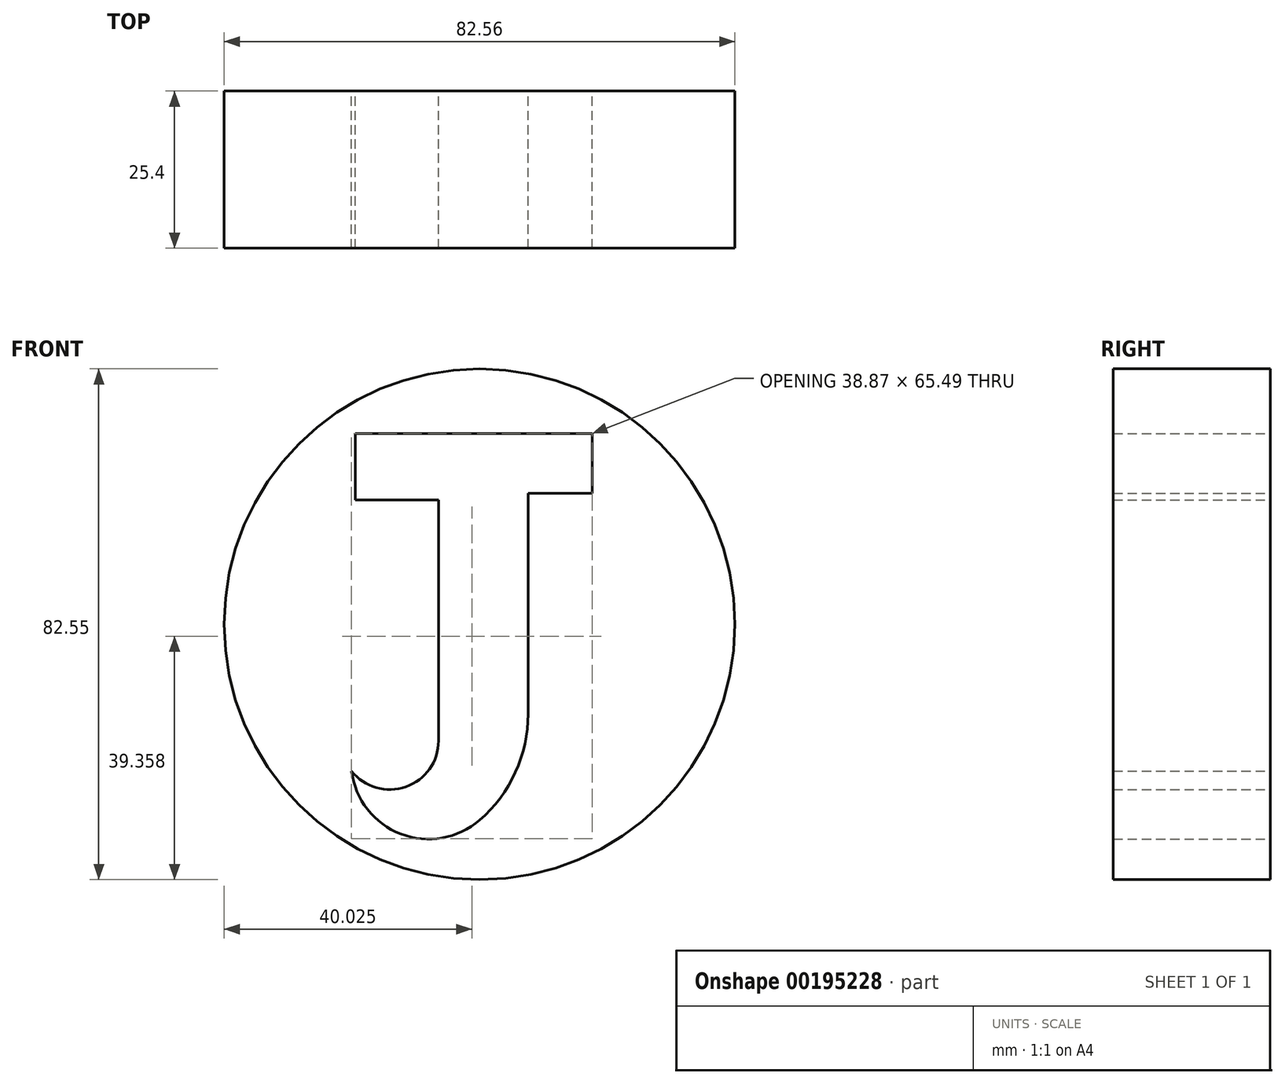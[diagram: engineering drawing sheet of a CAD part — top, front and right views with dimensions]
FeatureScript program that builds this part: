
annotation { "Feature Type Name" : "Feature", "Feature Type Description" : "" }
export const myFeature = defineFeature(function(context is Context, id is Id, definition is map)
    precondition{}
    {
        {
            var Q0;
            Q0=qCreatedBy(makeId("Front.planeOp"),FACE);
            var sketch = newSketch(context, id + "F0", { "sketchPlane" : qUnion([Q0])});
            skCircle(sketch, "E0", {"center": v(0, -3.42) * mm, "radius": 41.28 * mm});
            skSolve(sketch);
        }
        {
            var Q0;
            Q0 = qSketchRegion(id + "F0", true);
            extrude(context, id + "F1", {"entities" : qUnion([Q0]), "depth" : 25.4 * mm});
        }
        {
            var Q0;
            Q0=qCreatedBy(makeId("Front.planeOp"),FACE);
            var sketch = newSketch(context, id + "F2", { "sketchPlane" : qUnion([Q0])});
            skLineSegment(sketch, "E1", {"start": v(-20.1, 27.4) * mm, "end": v(18.18, 27.4) * mm});
            skLineSegment(sketch, "E2", {"start": v(18.18, 27.4) * mm, "end": v(18.18, 17.76) * mm});
            skLineSegment(sketch, "E3", {"start": v(-20.1, 27.4) * mm, "end": v(-20.1, 20.8) * mm});
            skLineSegment(sketch, "E4", {"start": v(-20.1, 27.4) * mm, "end": v(-20.1, 18.8) * mm});
            skLineSegment(sketch, "E5", {"start": v(-20.1, 27.4) * mm, "end": v(-20.1, 16.68) * mm});
            skLineSegment(sketch, "E6", {"start": v(-20.1, 16.68) * mm, "end": v(-6.64, 16.68) * mm});
            skLineSegment(sketch, "E7", {"start": v(18.18, 17.76) * mm, "end": v(7.85, 17.76) * mm});
            skLineSegment(sketch, "E8", {"start": v(-6.64, 16.68) * mm, "end": v(-6.64, 0) * mm});
            skLineSegment(sketch, "E9", {"start": v(7.85, 17.76) * mm, "end": v(7.85, 0) * mm});
            skLineSegment(sketch, "E10", {"start": v(7.85, 0) * mm, "end": v(7.85, -17.92) * mm});
            skLineSegment(sketch, "E11", {"start": v(-6.64, 0) * mm, "end": v(-6.64, -10.14) * mm});
            skArc(sketch, "E12", {"start": v(0, -35.09) * mm, "mid": v(5.8, -27.36) * mm, "end": v(7.85, -17.92) * mm});
            skArc(sketch, "E13", {"start": v(0, -35.09) * mm, "mid": v(-12.72, -37.32) * mm, "end": v(-20.69, -27.16) * mm});
            skLineSegment(sketch, "E14", {"start": v(-6.64, -10.14) * mm, "end": v(-6.64, -22.25) * mm});
            skArc(sketch, "E15", {"start": v(-6.64, -22.25) * mm, "mid": v(-11.92, -29.7) * mm, "end": v(-20.69, -27.16) * mm});
            skSolve(sketch);
        }
        {
            var Q0;
            Q0 = qSketchRegion(id + "F2", true);
            extrude(context, id + "F3", {"entities" : qUnion([Q0]), "operationType" : NewBodyOperationType.REMOVE, "endBound" : BoundingType.THROUGH_ALL, "depth" : 25.4 * mm});
        }
    });
